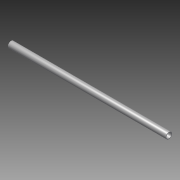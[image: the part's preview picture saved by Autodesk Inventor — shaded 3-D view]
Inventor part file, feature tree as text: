
AUTODESK INVENTOR PART (.ipt)
format: ipt  version: 2014 (Build 180170000, 170)  size: 99,840 bytes
history: native  units: in
note: dims shown in document units (in); Inventor stores cm internally (conversion verified against a paired STEP export)
features: other x2, extrude x1, imported_body x1, sketch x1
ambient origin geometry x8: Origin, YZ Plane, XZ Plane, XY Plane, X Axis, Y Axis, Z Axis, Center Point
bodies: Body1 (feature_tree)
feature tree (5):
  parser-record x1  (decoder bookkeeping rows leaked as tree rows — omitted from the tree; the rows remain in map.json)
  other  "4347K3111"
  extrude  "Extrusion1"  [1 undecoded]
  imported_body  "Base1"
  sketch  "Sketch1"  dims[d0=9.0in d1=0.0in]
note: 1 required parameter value undecoded (feature->parameter linkage not recoverable at this tier; creation-order binding heuristic only, values carry confidence <= 0.55)
